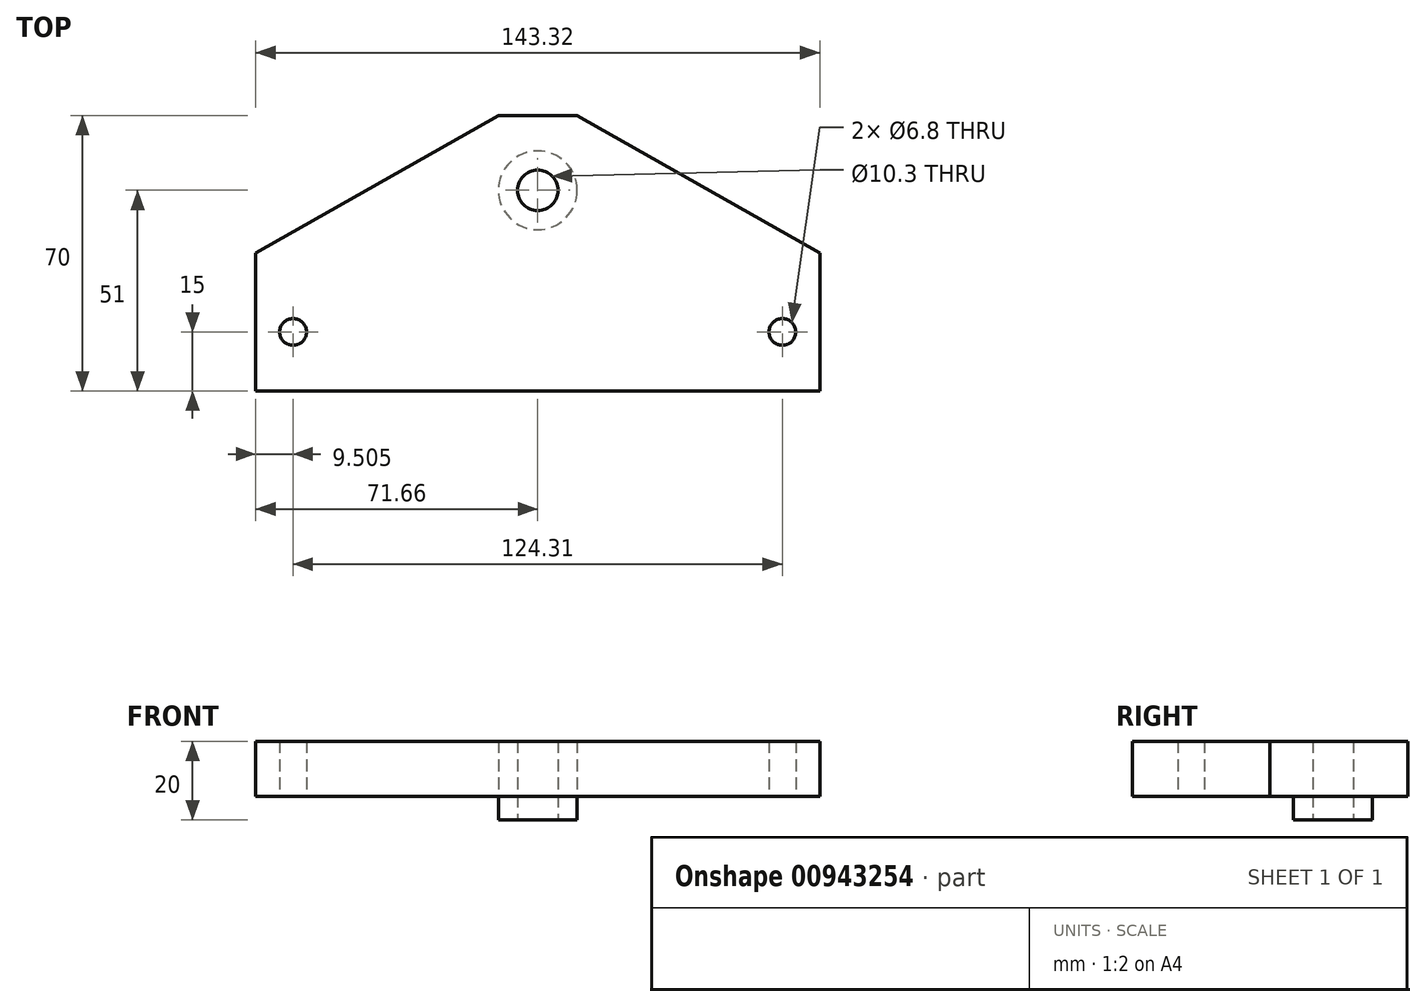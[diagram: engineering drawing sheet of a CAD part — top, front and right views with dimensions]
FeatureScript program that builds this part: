
annotation { "Feature Type Name" : "Feature", "Feature Type Description" : "" }
export const myFeature = defineFeature(function(context is Context, id is Id, definition is map)
    precondition{}
    {
        {
            var Q0;
            Q0=qCreatedBy(makeId("Top.planeOp"),FACE);
            var sketch = newSketch(context, id + "F0", { "sketchPlane" : qUnion([Q0])});
            skLineSegment(sketch, "E0", {"start": v(0, 0) * mm, "end": v(-62.16, 0) * mm, "construction": true});
            skLineSegment(sketch, "E1", {"start": v(0, 0) * mm, "end": v(62.16, 0) * mm, "construction": true});
            skLineSegment(sketch, "E2", {"start": v(0, 0) * mm, "end": v(-71.66, 0) * mm, "construction": true});
            skLineSegment(sketch, "E3", {"start": v(0, 0) * mm, "end": v(71.66, 0) * mm, "construction": true});
            skLineSegment(sketch, "E4", {"start": v(-71.66, 0) * mm, "end": v(-71.66, -15) * mm, "construction": true});
            skLineSegment(sketch, "E5.bottom", {"start": v(-71.66, -15) * mm, "end": v(71.66, -15) * mm});
            skLineSegment(sketch, "E5.top", {"start": v(-71.66, 20) * mm, "end": v(71.66, 20) * mm});
            skLineSegment(sketch, "E5.left", {"start": v(-71.66, -15) * mm, "end": v(-71.66, 20) * mm});
            skLineSegment(sketch, "E5.right", {"start": v(71.66, -15) * mm, "end": v(71.66, 20) * mm});
            skLineSegment(sketch, "E6", {"start": v(0, 0) * mm, "end": v(0, 55) * mm, "construction": true});
            skLineSegment(sketch, "E7", {"start": v(0, 55) * mm, "end": v(10, 55) * mm, "construction": true});
            skLineSegment(sketch, "E8", {"start": v(10, 55) * mm, "end": v(-10, 55) * mm, "construction": true});
            skLineSegment(sketch, "E9", {"start": v(0, 20) * mm, "end": v(0, 36) * mm, "construction": true});
            skLineSegment(sketch, "E10", {"start": v(-71.66, 20) * mm, "end": v(-10, 55) * mm});
            skLineSegment(sketch, "E11", {"start": v(-10, 55) * mm, "end": v(10, 55) * mm});
            skLineSegment(sketch, "E12", {"start": v(10, 55) * mm, "end": v(71.66, 20) * mm});
            skCircle(sketch, "E13", {"center": v(-62.16, 0) * mm, "radius": 3.4 * mm});
            skCircle(sketch, "E14", {"center": v(62.16, 0) * mm, "radius": 3.4 * mm});
            skCircle(sketch, "E15", {"center": v(0, 36) * mm, "radius": 5.15 * mm});
            skSolve(sketch);
        }
        {
            var Q0;
            Q0 = qSketchRegion(id + "F0", true);
            extrude(context, id + "F1", {"entities" : qUnion([Q0]), "depth" : 14 * mm, "offsetDistance" : 25 * mm});
        }
        {
            var Q0;
            Q0=makeQuery(id+"F1.opExtrude","CAP_FACE",FACE,{"disambiguationData":[OSD([sQuery(id+"F0.wireOp",EDGE,"E5.bottom"),sQuery(id+"F0.wireOp",EDGE,"E5.left"),sQuery(id+"F0.wireOp",EDGE,"E5.right"),sQuery(id+"F0.wireOp",EDGE,"E10"),sQuery(id+"F0.wireOp",EDGE,"E11"),sQuery(id+"F0.wireOp",EDGE,"E12"),sQuery(id+"F0.wireOp",EDGE,"E13"),sQuery(id+"F0.wireOp",EDGE,"E14"),sQuery(id+"F0.wireOp",EDGE,"E15")])],"isStart":true});
            var sketch = newSketch(context, id + "F2", { "sketchPlane" : qUnion([Q0])});
            skCircle(sketch, "E16", {"center": v(0, -36) * mm, "radius": 10 * mm});
            skCircle(sketch, "E17", {"center": v(0, -36) * mm, "radius": 5.15 * mm});
            skSolve(sketch);
        }
        {
            var Q0;
            Q0 = qSketchRegion(id + "F2", true);
            extrude(context, id + "F3", {"entities" : qUnion([Q0]), "operationType" : NewBodyOperationType.ADD, "depth" : 6 * mm, "offsetDistance" : 25 * mm});
        }
    });
